# Revit family: Sanitary_Taps-Mixers_hansgrohe_71576007-Vernis-Blend-Single-lever-basin_
name_source: partatom
category: Plumbing Fixtures
revit_build: Autodesk Revit 2015 (Build: 20140322_1515(x64)
units: mm (PartAtom-declared; Revit-internal decimal feet)

## types (1)
- Chrome 000
    BIMobject category = Taps & Mixers
    BIMobject category code = sanitary-taps-mixers
    BIMobject main category = Sanitary
    BIMobject main category code = sanitary
    Brand url = http://www.hansgrohe-int.com
    Default Elevation = 1219.2 mm  [stored 4 ft]
    Design country = Germany
    Edition number = 1
    GTIN code = https://4059625293461
    IFC Classification = Sanitary Terminal
    Manufacturer country = Germany
    Manufacturer name = hansgrohe
    Material main = Chrome
    Product Guid = 2740fde1-51b0-4a6c-ac05-cfcc2242ff07
    Product SKU = 71576007
    Product certification = https://www.hansgrohe.com.cn
    Product data url = https://bimobject.com
    Product family = Basin mixers
    Product group = Vernis Blend
    Product name = 71576007 Vernis Blend Single lever basin mixer for concealed installation wall-mounted with spout 20,4 cm
    Product url = https://www.hansgrohe.com.cn
    QR code = http://bimobject.com
    Technical description = https://www.hansgrohe.com.cn

note: [stored X ft] marks values corroborated as IEEE doubles in the binary element streams (Revit-internal decimal feet)

## geometry (parser evidence)
native form markers: Blend x6, Sweep x2
no freeform markers — native parametric forms only
